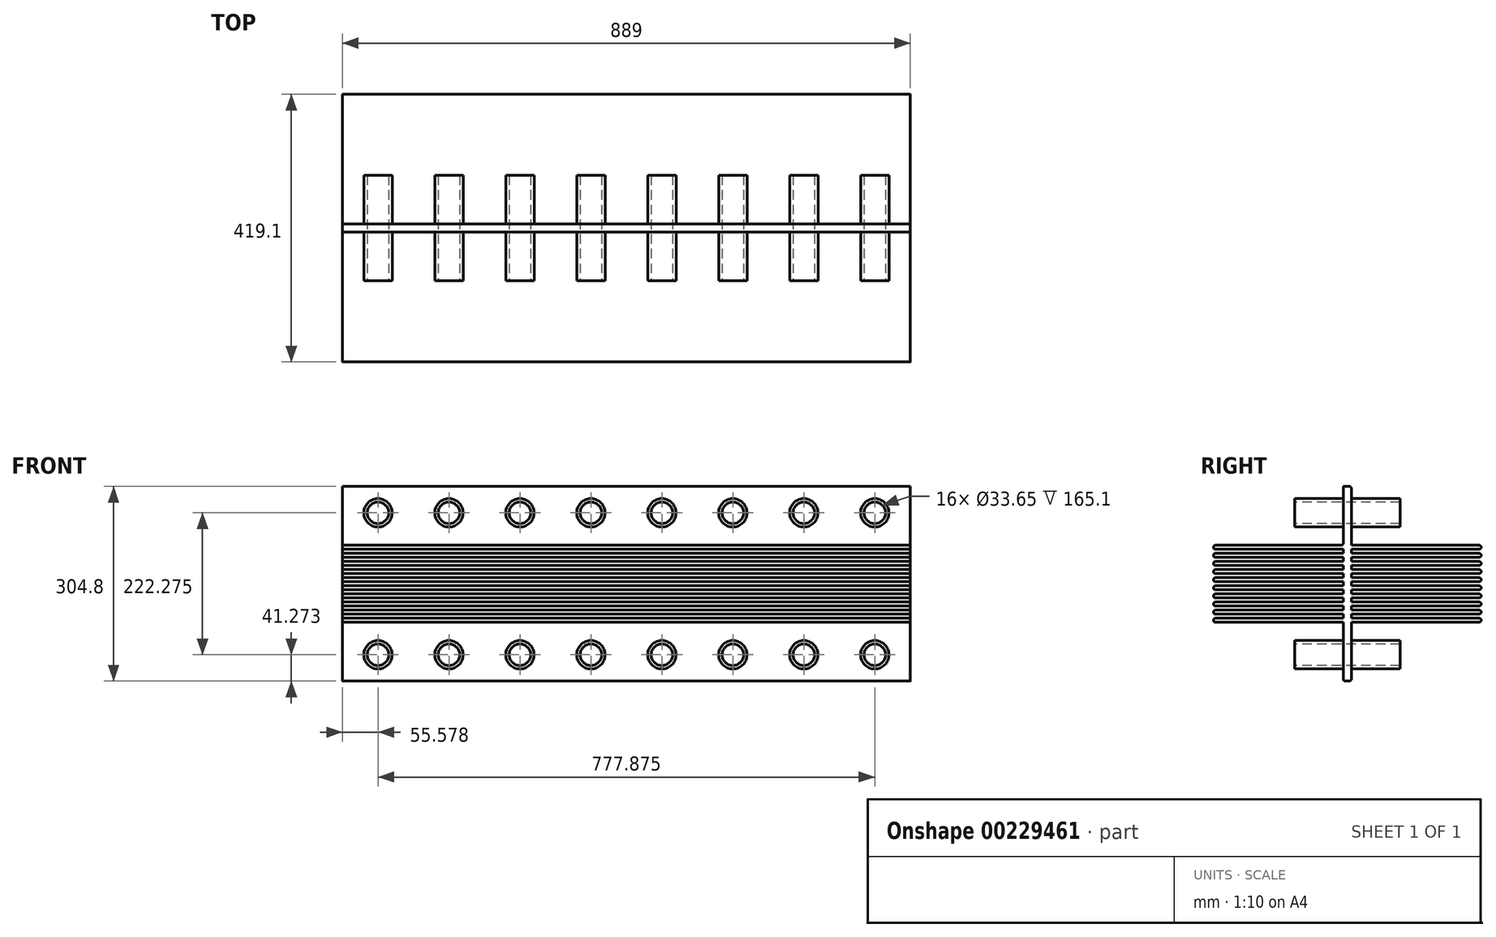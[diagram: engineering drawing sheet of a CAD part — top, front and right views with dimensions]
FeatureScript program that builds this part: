
annotation { "Feature Type Name" : "Feature", "Feature Type Description" : "" }
export const myFeature = defineFeature(function(context is Context, id is Id, definition is map)
    precondition{}
    {
        {
            var Q0;
            Q0=qCreatedBy(makeId("Front.planeOp"),FACE);
            var sketch = newSketch(context, id + "F0", { "sketchPlane" : qUnion([Q0])});
            skLineSegment(sketch, "E0.bottom", {"start": v(-681.77, 148.66) * mm, "end": v(207.23, 148.66) * mm});
            skLineSegment(sketch, "E0.top", {"start": v(-681.77, -156.14) * mm, "end": v(207.23, -156.14) * mm});
            skLineSegment(sketch, "E0.left", {"start": v(-681.77, 148.66) * mm, "end": v(-681.77, -156.14) * mm});
            skLineSegment(sketch, "E0.right", {"start": v(207.23, 148.66) * mm, "end": v(207.23, -156.14) * mm});
            skSolve(sketch);
        }
        {
            var Q0;
            Q0=makeQuery(id+"F0.imprint","IMPRINT",FACE,{"disambiguationData":[TD([[makeQuery(id+"F0.imprint","IMPRINT",EDGE,{"derivedFrom":sQuery(id+"F0.wireOp",EDGE,"E0.bottom")}),-1.0]])]});
            extrude(context, id + "F1", {"entities" : qUnion([Q0]), "depth" : 12.7 * mm});
        }
        {
            var Q0;
            Q0=makeQuery(id+"F1.opExtrude","CAP_FACE",FACE,{"disambiguationData":[OSD([sQuery(id+"F0.wireOp",EDGE,"E0.bottom"),sQuery(id+"F0.wireOp",EDGE,"E0.top"),sQuery(id+"F0.wireOp",EDGE,"E0.left"),sQuery(id+"F0.wireOp",EDGE,"E0.right")])],"isStart":false});
            var sketch = newSketch(context, id + "F2", { "sketchPlane" : qUnion([Q0])});
            skPoint(sketch, "E1", {"position": v(-626.2, -114.87) * mm});
            skPoint(sketch, "E2.0.1.0", {"position": v(-626.2, 107.4) * mm});
            skPoint(sketch, "E2.1.0.0", {"position": v(-515.07, -114.87) * mm});
            skPoint(sketch, "E2.1.1.0", {"position": v(-515.07, 107.4) * mm});
            skPoint(sketch, "E2.2.0.0", {"position": v(-403.94, -114.87) * mm});
            skPoint(sketch, "E2.2.1.0", {"position": v(-403.94, 107.4) * mm});
            skPoint(sketch, "E2.3.0.0", {"position": v(-292.82, -114.87) * mm});
            skPoint(sketch, "E2.3.1.0", {"position": v(-292.82, 107.4) * mm});
            skPoint(sketch, "E2.4.0.0", {"position": v(-181.7, -114.87) * mm});
            skPoint(sketch, "E2.4.1.0", {"position": v(-181.7, 107.4) * mm});
            skPoint(sketch, "E2.5.0.0", {"position": v(-70.57, -114.87) * mm});
            skPoint(sketch, "E2.5.1.0", {"position": v(-70.57, 107.4) * mm});
            skPoint(sketch, "E2.6.0.0", {"position": v(40.56, -114.87) * mm});
            skPoint(sketch, "E2.6.1.0", {"position": v(40.56, 107.4) * mm});
            skPoint(sketch, "E2.7.0.0", {"position": v(151.68, -114.87) * mm});
            skPoint(sketch, "E2.7.1.0", {"position": v(151.68, 107.4) * mm});
            skLineSegment(sketch, "E2.direction1", {"start": v(-626.2, -114.87) * mm, "end": v(-515.07, -114.87) * mm, "construction": true});
            skLineSegment(sketch, "E2.direction2", {"start": v(-626.2, -114.87) * mm, "end": v(-626.2, 107.4) * mm, "construction": true});
            skSolve(sketch);
        }
        {
            var Q0;
            Q0=sQuery(id+"F2.wireOp",VERTEX,"E2.0.1.0");
            var Q1;
            Q1=sQuery(id+"F2.wireOp",VERTEX,"E2.1.1.0");
            var Q2;
            Q2=sQuery(id+"F2.wireOp",VERTEX,"E2.2.1.0");
            var Q3;
            Q3=sQuery(id+"F2.wireOp",VERTEX,"E2.3.1.0");
            var Q4;
            Q4=sQuery(id+"F2.wireOp",VERTEX,"E2.4.1.0");
            var Q5;
            Q5=sQuery(id+"F2.wireOp",VERTEX,"E2.5.1.0");
            var Q6;
            Q6=sQuery(id+"F2.wireOp",VERTEX,"E2.6.1.0");
            var Q7;
            Q7=sQuery(id+"F2.wireOp",VERTEX,"E2.7.1.0");
            var Q8;
            Q8=sQuery(id+"F2.wireOp",VERTEX,"E2.7.0.0");
            var Q9;
            Q9=sQuery(id+"F2.wireOp",VERTEX,"E2.6.0.0");
            var Q10;
            Q10=sQuery(id+"F2.wireOp",VERTEX,"E2.5.0.0");
            var Q11;
            Q11=sQuery(id+"F2.wireOp",VERTEX,"E2.4.0.0");
            var Q12;
            Q12=sQuery(id+"F2.wireOp",VERTEX,"E2.3.0.0");
            var Q13;
            Q13=sQuery(id+"F2.wireOp",VERTEX,"E2.2.0.0");
            var Q14;
            Q14=sQuery(id+"F2.wireOp",VERTEX,"E1");
            var Q15;
            Q15=sQuery(id+"F2.wireOp",VERTEX,"E2.1.0.0");
            var Q16;
            Q16=makeQuery(id+"F1.opExtrude","SWEPT_BODY",BODY,{"disambiguationData":[OSD([sQuery(id+"F0.wireOp",EDGE,"E0.bottom"),sQuery(id+"F0.wireOp",EDGE,"E0.top"),sQuery(id+"F0.wireOp",EDGE,"E0.left"),sQuery(id+"F0.wireOp",EDGE,"E0.right")])]});
            hole(context, id + "F3", {"style" : HoleStyle.SIMPLE, "endStyle" : HoleEndStyle.THROUGH, "holeDiameter" : 33.65 * mm, "locations" : qUnion([Q0, Q1, Q2, Q3, Q4, Q5, Q6, Q7, Q8, Q9, Q10, Q11, Q12, Q13, Q14, Q15]), "scope" : qUnion([Q16]), "isTappedThrough" : true});
        }
        {
            var Q0;
            Q0=makeQuery(id+"F1.opExtrude","SWEPT_FACE",FACE,{"disambiguationData":[OSD([sQuery(id+"F0.wireOp",EDGE,"E0.right")])]});
            var sketch = newSketch(context, id + "F4", { "sketchPlane" : qUnion([Q0])});
            skLineSegment(sketch, "E3", {"start": v(-6.35, -156.14) * mm, "end": v(-6.35, 148.66) * mm, "construction": true});
            skLineSegment(sketch, "E4", {"start": v(-12.7, -3.74) * mm, "end": v(-116.38, -3.74) * mm, "construction": true});
            skLineSegment(sketch, "E5.bottom", {"start": v(-12.7, -6.92) * mm, "end": v(-212.72, -6.92) * mm});
            skLineSegment(sketch, "E5.top", {"start": v(-12.7, -13.27) * mm, "end": v(-212.72, -13.27) * mm});
            skLineSegment(sketch, "E5.left", {"start": v(-12.7, -6.92) * mm, "end": v(-12.7, -13.27) * mm});
            skLineSegment(sketch, "E5.right", {"start": v(-215.9, -10.1) * mm, "end": v(-215.9, -10.1) * mm});
            skLineSegment(sketch, "E6.bottom", {"start": v(-12.7, -19.62) * mm, "end": v(-212.72, -19.62) * mm});
            skLineSegment(sketch, "E6.top", {"start": v(-12.7, -25.97) * mm, "end": v(-212.72, -25.97) * mm});
            skLineSegment(sketch, "E6.left", {"start": v(-12.7, -19.62) * mm, "end": v(-12.7, -25.97) * mm});
            skLineSegment(sketch, "E6.right", {"start": v(-215.9, -22.8) * mm, "end": v(-215.9, -22.8) * mm});
            skLineSegment(sketch, "E7.bottom", {"start": v(-12.7, -32.32) * mm, "end": v(-212.72, -32.32) * mm});
            skLineSegment(sketch, "E7.top", {"start": v(-12.7, -38.67) * mm, "end": v(-212.72, -38.67) * mm});
            skLineSegment(sketch, "E7.left", {"start": v(-12.7, -32.32) * mm, "end": v(-12.7, -38.67) * mm});
            skLineSegment(sketch, "E7.right", {"start": v(-215.9, -35.5) * mm, "end": v(-215.9, -35.5) * mm});
            skLineSegment(sketch, "E8.bottom", {"start": v(-12.7, -45.02) * mm, "end": v(-212.72, -45.02) * mm});
            skLineSegment(sketch, "E8.top", {"start": v(-12.7, -51.37) * mm, "end": v(-212.72, -51.37) * mm});
            skLineSegment(sketch, "E8.left", {"start": v(-12.7, -45.02) * mm, "end": v(-12.7, -51.37) * mm});
            skLineSegment(sketch, "E8.right", {"start": v(-215.9, -48.2) * mm, "end": v(-215.9, -48.2) * mm});
            skLineSegment(sketch, "E9.bottom", {"start": v(-12.7, -57.72) * mm, "end": v(-212.72, -57.72) * mm});
            skLineSegment(sketch, "E9.top", {"start": v(-12.7, -64.07) * mm, "end": v(-212.72, -64.07) * mm});
            skLineSegment(sketch, "E9.left", {"start": v(-12.7, -57.72) * mm, "end": v(-12.7, -64.07) * mm});
            skLineSegment(sketch, "E9.right", {"start": v(-215.9, -60.9) * mm, "end": v(-215.9, -60.9) * mm});
            skLineSegment(sketch, "E10.MirrorCS", {"start": v(-12.7, -0.57) * mm, "end": v(-212.72, -0.57) * mm});
            skLineSegment(sketch, "E11.MirrorCS", {"start": v(-12.7, 5.78) * mm, "end": v(-212.72, 5.78) * mm});
            skLineSegment(sketch, "E12.MirrorCS", {"start": v(-215.9, 2.6) * mm, "end": v(-215.9, 2.6) * mm});
            skLineSegment(sketch, "E13.MirrorCS", {"start": v(-12.7, -0.57) * mm, "end": v(-12.7, 5.78) * mm});
            skLineSegment(sketch, "E14.MirrorCS", {"start": v(-12.7, 12.13) * mm, "end": v(-12.7, 18.48) * mm});
            skLineSegment(sketch, "E15.MirrorCS", {"start": v(-12.7, 12.13) * mm, "end": v(-212.72, 12.13) * mm});
            skLineSegment(sketch, "E16.MirrorCS", {"start": v(-12.7, 18.48) * mm, "end": v(-212.72, 18.48) * mm});
            skLineSegment(sketch, "E17.MirrorCS", {"start": v(-12.7, 24.83) * mm, "end": v(-212.72, 24.83) * mm});
            skLineSegment(sketch, "E18.MirrorCS", {"start": v(-12.7, 31.18) * mm, "end": v(-212.72, 31.18) * mm});
            skLineSegment(sketch, "E19.MirrorCS", {"start": v(-12.7, 24.83) * mm, "end": v(-12.7, 31.18) * mm});
            skLineSegment(sketch, "E20.MirrorCS", {"start": v(-12.7, 37.53) * mm, "end": v(-212.72, 37.53) * mm});
            skLineSegment(sketch, "E21.MirrorCS", {"start": v(-12.7, 43.88) * mm, "end": v(-212.72, 43.88) * mm});
            skLineSegment(sketch, "E22.MirrorCS", {"start": v(-12.7, 37.53) * mm, "end": v(-12.7, 43.88) * mm});
            skLineSegment(sketch, "E23.MirrorCS", {"start": v(-12.7, 50.23) * mm, "end": v(-12.7, 56.58) * mm});
            skLineSegment(sketch, "E24.MirrorCS", {"start": v(-12.7, 50.23) * mm, "end": v(-212.72, 50.23) * mm});
            skLineSegment(sketch, "E25.MirrorCS", {"start": v(-12.7, 56.58) * mm, "end": v(-212.72, 56.58) * mm});
            skLineSegment(sketch, "E26.MirrorCS", {"start": v(-215.9, 15.3) * mm, "end": v(-215.9, 15.3) * mm});
            skLineSegment(sketch, "E27.MirrorCS", {"start": v(-215.9, 28) * mm, "end": v(-215.9, 28) * mm});
            skLineSegment(sketch, "E28.MirrorCS", {"start": v(-215.9, 40.7) * mm, "end": v(-215.9, 40.7) * mm});
            skLineSegment(sketch, "E29.MirrorCS", {"start": v(-215.9, 53.4) * mm, "end": v(-215.9, 53.4) * mm});
            skLineSegment(sketch, "E30.MirrorCS", {"start": v(0, 56.58) * mm, "end": v(200.02, 56.58) * mm});
            skLineSegment(sketch, "E31.MirrorCS", {"start": v(0, 50.23) * mm, "end": v(200.03, 50.23) * mm});
            skLineSegment(sketch, "E32.MirrorCS", {"start": v(0, 43.88) * mm, "end": v(200.02, 43.88) * mm});
            skLineSegment(sketch, "E33.MirrorCS", {"start": v(0, 37.53) * mm, "end": v(200.02, 37.53) * mm});
            skLineSegment(sketch, "E34.MirrorCS", {"start": v(0, 31.18) * mm, "end": v(200.02, 31.18) * mm});
            skLineSegment(sketch, "E35.MirrorCS", {"start": v(0, 24.83) * mm, "end": v(200.02, 24.83) * mm});
            skLineSegment(sketch, "E36.MirrorCS", {"start": v(0, 18.48) * mm, "end": v(200.02, 18.48) * mm});
            skLineSegment(sketch, "E37.MirrorCS", {"start": v(0, 12.13) * mm, "end": v(200.02, 12.13) * mm});
            skLineSegment(sketch, "E38.MirrorCS", {"start": v(0, 5.78) * mm, "end": v(200.02, 5.78) * mm});
            skLineSegment(sketch, "E39.MirrorCS", {"start": v(0, -0.57) * mm, "end": v(200.03, -0.57) * mm});
            skLineSegment(sketch, "E40.MirrorCS", {"start": v(0, -6.92) * mm, "end": v(200.03, -6.92) * mm});
            skLineSegment(sketch, "E41.MirrorCS", {"start": v(0, -13.27) * mm, "end": v(200.02, -13.27) * mm});
            skLineSegment(sketch, "E42.MirrorCS", {"start": v(0, -25.97) * mm, "end": v(200.02, -25.97) * mm});
            skLineSegment(sketch, "E43.MirrorCS", {"start": v(0, -19.62) * mm, "end": v(200.02, -19.62) * mm});
            skLineSegment(sketch, "E44.MirrorCS", {"start": v(0, -32.32) * mm, "end": v(200.02, -32.32) * mm});
            skLineSegment(sketch, "E45.MirrorCS", {"start": v(0, -38.67) * mm, "end": v(200.02, -38.67) * mm});
            skLineSegment(sketch, "E46.MirrorCS", {"start": v(0, -45.02) * mm, "end": v(200.02, -45.02) * mm});
            skLineSegment(sketch, "E47.MirrorCS", {"start": v(0, -51.37) * mm, "end": v(200.03, -51.37) * mm});
            skLineSegment(sketch, "E48.MirrorCS", {"start": v(0, -57.72) * mm, "end": v(200.03, -57.72) * mm});
            skLineSegment(sketch, "E49.MirrorCS", {"start": v(0, -64.07) * mm, "end": v(200.02, -64.07) * mm});
            skLineSegment(sketch, "E50.MirrorCS", {"start": v(203.2, 53.4) * mm, "end": v(203.2, 53.4) * mm});
            skLineSegment(sketch, "E51.MirrorCS", {"start": v(203.2, 40.7) * mm, "end": v(203.2, 40.7) * mm});
            skLineSegment(sketch, "E52.MirrorCS", {"start": v(203.2, 28) * mm, "end": v(203.2, 28) * mm});
            skLineSegment(sketch, "E53.MirrorCS", {"start": v(203.2, 15.3) * mm, "end": v(203.2, 15.3) * mm});
            skLineSegment(sketch, "E54.MirrorCS", {"start": v(203.2, 2.6) * mm, "end": v(203.2, 2.6) * mm});
            skLineSegment(sketch, "E55.MirrorCS", {"start": v(203.2, -10.1) * mm, "end": v(203.2, -10.1) * mm});
            skLineSegment(sketch, "E56.MirrorCS", {"start": v(203.2, -22.8) * mm, "end": v(203.2, -22.8) * mm});
            skLineSegment(sketch, "E57.MirrorCS", {"start": v(203.2, -35.5) * mm, "end": v(203.2, -35.5) * mm});
            skLineSegment(sketch, "E58.MirrorCS", {"start": v(203.2, -48.2) * mm, "end": v(203.2, -48.2) * mm});
            skLineSegment(sketch, "E59.MirrorCS", {"start": v(203.2, -60.9) * mm, "end": v(203.2, -60.9) * mm});
            skLineSegment(sketch, "E60.MirrorCS", {"start": v(0, 50.23) * mm, "end": v(0, 56.58) * mm});
            skLineSegment(sketch, "E61.MirrorCS", {"start": v(0, 37.53) * mm, "end": v(0, 43.88) * mm});
            skLineSegment(sketch, "E62.MirrorCS", {"start": v(0, 24.83) * mm, "end": v(0, 31.18) * mm});
            skLineSegment(sketch, "E63.MirrorCS", {"start": v(0, 12.13) * mm, "end": v(0, 18.48) * mm});
            skLineSegment(sketch, "E64.MirrorCS", {"start": v(0, -0.57) * mm, "end": v(0, 5.78) * mm});
            skLineSegment(sketch, "E65.MirrorCS", {"start": v(0, -6.92) * mm, "end": v(0, -13.27) * mm});
            skLineSegment(sketch, "E66.MirrorCS", {"start": v(0, -19.62) * mm, "end": v(0, -25.97) * mm});
            skLineSegment(sketch, "E67.MirrorCS", {"start": v(0, -32.32) * mm, "end": v(0, -38.67) * mm});
            skLineSegment(sketch, "E68.MirrorCS", {"start": v(0, -45.02) * mm, "end": v(0, -51.37) * mm});
            skLineSegment(sketch, "E69.MirrorCS", {"start": v(0, -57.72) * mm, "end": v(0, -64.07) * mm});
            skPoint(sketch, "E70.visualSharp", {"position": v(203.2, 56.58) * mm});
            skArc(sketch, "E70.filletArc", {"start": v(203.2, 53.4) * mm, "mid": v(202.27, 55.65) * mm, "end": v(200.02, 56.58) * mm});
            skPoint(sketch, "E71.visualSharp", {"position": v(203.2, 50.23) * mm});
            skArc(sketch, "E71.filletArc", {"start": v(200.03, 50.23) * mm, "mid": v(202.27, 51.16) * mm, "end": v(203.2, 53.4) * mm});
            skPoint(sketch, "E72.visualSharp", {"position": v(203.2, 43.88) * mm});
            skArc(sketch, "E72.filletArc", {"start": v(203.2, 40.7) * mm, "mid": v(202.27, 42.95) * mm, "end": v(200.02, 43.88) * mm});
            skPoint(sketch, "E73.visualSharp", {"position": v(203.2, 37.53) * mm});
            skArc(sketch, "E73.filletArc", {"start": v(200.02, 37.53) * mm, "mid": v(202.27, 38.46) * mm, "end": v(203.2, 40.7) * mm});
            skPoint(sketch, "E74.visualSharp", {"position": v(203.2, 31.18) * mm});
            skArc(sketch, "E74.filletArc", {"start": v(203.2, 28) * mm, "mid": v(202.27, 30.25) * mm, "end": v(200.02, 31.18) * mm});
            skPoint(sketch, "E75.visualSharp", {"position": v(203.2, 24.83) * mm});
            skArc(sketch, "E75.filletArc", {"start": v(200.02, 24.83) * mm, "mid": v(202.27, 25.76) * mm, "end": v(203.2, 28) * mm});
            skPoint(sketch, "E76.visualSharp", {"position": v(203.2, 18.48) * mm});
            skArc(sketch, "E76.filletArc", {"start": v(203.2, 15.3) * mm, "mid": v(202.27, 17.55) * mm, "end": v(200.02, 18.48) * mm});
            skPoint(sketch, "E77.visualSharp", {"position": v(203.2, 12.13) * mm});
            skArc(sketch, "E77.filletArc", {"start": v(200.02, 12.13) * mm, "mid": v(202.27, 13.06) * mm, "end": v(203.2, 15.3) * mm});
            skPoint(sketch, "E78.visualSharp", {"position": v(203.2, 5.78) * mm});
            skArc(sketch, "E78.filletArc", {"start": v(203.2, 2.6) * mm, "mid": v(202.27, 4.85) * mm, "end": v(200.02, 5.78) * mm});
            skPoint(sketch, "E79.visualSharp", {"position": v(203.2, -0.57) * mm});
            skArc(sketch, "E79.filletArc", {"start": v(200.03, -0.57) * mm, "mid": v(202.27, 0.36) * mm, "end": v(203.2, 2.6) * mm});
            skPoint(sketch, "E80.visualSharp", {"position": v(203.2, -6.92) * mm});
            skArc(sketch, "E80.filletArc", {"start": v(203.2, -10.1) * mm, "mid": v(202.27, -7.85) * mm, "end": v(200.03, -6.92) * mm});
            skPoint(sketch, "E81.visualSharp", {"position": v(203.2, -13.27) * mm});
            skArc(sketch, "E81.filletArc", {"start": v(200.02, -13.27) * mm, "mid": v(202.27, -12.34) * mm, "end": v(203.2, -10.1) * mm});
            skPoint(sketch, "E82.visualSharp", {"position": v(203.2, -19.62) * mm});
            skArc(sketch, "E82.filletArc", {"start": v(203.2, -22.8) * mm, "mid": v(202.27, -20.55) * mm, "end": v(200.02, -19.62) * mm});
            skPoint(sketch, "E83.visualSharp", {"position": v(203.2, -25.97) * mm});
            skArc(sketch, "E83.filletArc", {"start": v(200.02, -25.97) * mm, "mid": v(202.27, -25.04) * mm, "end": v(203.2, -22.8) * mm});
            skPoint(sketch, "E84.visualSharp", {"position": v(203.2, -32.32) * mm});
            skArc(sketch, "E84.filletArc", {"start": v(203.2, -35.5) * mm, "mid": v(202.27, -33.25) * mm, "end": v(200.02, -32.32) * mm});
            skPoint(sketch, "E85.visualSharp", {"position": v(203.2, -38.67) * mm});
            skArc(sketch, "E85.filletArc", {"start": v(200.02, -38.67) * mm, "mid": v(202.27, -37.74) * mm, "end": v(203.2, -35.5) * mm});
            skPoint(sketch, "E86.visualSharp", {"position": v(203.2, -45.02) * mm});
            skArc(sketch, "E86.filletArc", {"start": v(203.2, -48.2) * mm, "mid": v(202.27, -45.95) * mm, "end": v(200.02, -45.02) * mm});
            skPoint(sketch, "E87.visualSharp", {"position": v(203.2, -51.37) * mm});
            skArc(sketch, "E87.filletArc", {"start": v(200.03, -51.37) * mm, "mid": v(202.27, -50.44) * mm, "end": v(203.2, -48.2) * mm});
            skPoint(sketch, "E88.visualSharp", {"position": v(203.2, -57.72) * mm});
            skArc(sketch, "E88.filletArc", {"start": v(203.2, -60.9) * mm, "mid": v(202.27, -58.65) * mm, "end": v(200.03, -57.72) * mm});
            skPoint(sketch, "E89.visualSharp", {"position": v(203.2, -64.07) * mm});
            skArc(sketch, "E89.filletArc", {"start": v(200.02, -64.07) * mm, "mid": v(202.27, -63.14) * mm, "end": v(203.2, -60.9) * mm});
            skPoint(sketch, "E90.visualSharp", {"position": v(-215.9, 56.58) * mm});
            skArc(sketch, "E90.filletArc", {"start": v(-212.72, 56.58) * mm, "mid": v(-214.97, 55.65) * mm, "end": v(-215.9, 53.4) * mm});
            skPoint(sketch, "E91.visualSharp", {"position": v(-215.9, 50.23) * mm});
            skArc(sketch, "E91.filletArc", {"start": v(-215.9, 53.4) * mm, "mid": v(-214.97, 51.16) * mm, "end": v(-212.72, 50.23) * mm});
            skPoint(sketch, "E92.visualSharp", {"position": v(-215.9, 43.88) * mm});
            skArc(sketch, "E92.filletArc", {"start": v(-212.72, 43.88) * mm, "mid": v(-214.97, 42.95) * mm, "end": v(-215.9, 40.7) * mm});
            skPoint(sketch, "E93.visualSharp", {"position": v(-215.9, 37.53) * mm});
            skArc(sketch, "E93.filletArc", {"start": v(-215.9, 40.7) * mm, "mid": v(-214.97, 38.46) * mm, "end": v(-212.72, 37.53) * mm});
            skPoint(sketch, "E94.visualSharp", {"position": v(-215.9, 31.18) * mm});
            skArc(sketch, "E94.filletArc", {"start": v(-212.72, 31.18) * mm, "mid": v(-214.97, 30.25) * mm, "end": v(-215.9, 28) * mm});
            skPoint(sketch, "E95.visualSharp", {"position": v(-215.9, 24.83) * mm});
            skArc(sketch, "E95.filletArc", {"start": v(-215.9, 28) * mm, "mid": v(-214.97, 25.76) * mm, "end": v(-212.72, 24.83) * mm});
            skPoint(sketch, "E96.visualSharp", {"position": v(-215.9, 18.48) * mm});
            skArc(sketch, "E96.filletArc", {"start": v(-212.72, 18.48) * mm, "mid": v(-214.97, 17.55) * mm, "end": v(-215.9, 15.3) * mm});
            skPoint(sketch, "E97.visualSharp", {"position": v(-215.9, 12.13) * mm});
            skArc(sketch, "E97.filletArc", {"start": v(-215.9, 15.3) * mm, "mid": v(-214.97, 13.06) * mm, "end": v(-212.72, 12.13) * mm});
            skPoint(sketch, "E98.visualSharp", {"position": v(-215.9, 5.78) * mm});
            skArc(sketch, "E98.filletArc", {"start": v(-212.72, 5.78) * mm, "mid": v(-214.97, 4.85) * mm, "end": v(-215.9, 2.6) * mm});
            skPoint(sketch, "E99.visualSharp", {"position": v(-215.9, -0.57) * mm});
            skArc(sketch, "E99.filletArc", {"start": v(-215.9, 2.6) * mm, "mid": v(-214.97, 0.36) * mm, "end": v(-212.72, -0.57) * mm});
            skPoint(sketch, "E100.visualSharp", {"position": v(-215.9, -6.92) * mm});
            skArc(sketch, "E100.filletArc", {"start": v(-212.72, -6.92) * mm, "mid": v(-214.97, -7.85) * mm, "end": v(-215.9, -10.1) * mm});
            skPoint(sketch, "E101.visualSharp", {"position": v(-215.9, -13.27) * mm});
            skArc(sketch, "E101.filletArc", {"start": v(-215.9, -10.1) * mm, "mid": v(-214.97, -12.34) * mm, "end": v(-212.72, -13.27) * mm});
            skPoint(sketch, "E102.visualSharp", {"position": v(-215.9, -19.62) * mm});
            skArc(sketch, "E102.filletArc", {"start": v(-212.72, -19.62) * mm, "mid": v(-214.97, -20.55) * mm, "end": v(-215.9, -22.8) * mm});
            skPoint(sketch, "E103.visualSharp", {"position": v(-215.9, -25.97) * mm});
            skArc(sketch, "E103.filletArc", {"start": v(-215.9, -22.8) * mm, "mid": v(-214.97, -25.04) * mm, "end": v(-212.72, -25.97) * mm});
            skPoint(sketch, "E104.visualSharp", {"position": v(-215.9, -38.67) * mm});
            skArc(sketch, "E104.filletArc", {"start": v(-215.9, -35.5) * mm, "mid": v(-214.97, -37.74) * mm, "end": v(-212.72, -38.67) * mm});
            skPoint(sketch, "E105.visualSharp", {"position": v(-215.9, -32.32) * mm});
            skArc(sketch, "E105.filletArc", {"start": v(-212.72, -32.32) * mm, "mid": v(-214.97, -33.25) * mm, "end": v(-215.9, -35.5) * mm});
            skPoint(sketch, "E106.visualSharp", {"position": v(-215.9, -45.02) * mm});
            skArc(sketch, "E106.filletArc", {"start": v(-212.72, -45.02) * mm, "mid": v(-214.97, -45.95) * mm, "end": v(-215.9, -48.2) * mm});
            skPoint(sketch, "E107.visualSharp", {"position": v(-215.9, -51.37) * mm});
            skArc(sketch, "E107.filletArc", {"start": v(-215.9, -48.2) * mm, "mid": v(-214.97, -50.44) * mm, "end": v(-212.72, -51.37) * mm});
            skPoint(sketch, "E108.visualSharp", {"position": v(-215.9, -57.72) * mm});
            skArc(sketch, "E108.filletArc", {"start": v(-212.72, -57.72) * mm, "mid": v(-214.97, -58.65) * mm, "end": v(-215.9, -60.9) * mm});
            skPoint(sketch, "E109.visualSharp", {"position": v(-215.9, -64.07) * mm});
            skArc(sketch, "E109.filletArc", {"start": v(-215.9, -60.9) * mm, "mid": v(-214.97, -63.14) * mm, "end": v(-212.72, -64.07) * mm});
            skSolve(sketch);
        }
        {
            var Q0;
            Q0 = qSketchRegion(id + "F4", true);
            extrude(context, id + "F5", {"entities" : qUnion([Q0]), "operationType" : NewBodyOperationType.ADD, "oppositeDirection" : true, "depth" : 889 * mm});
        }
        {
            var Q0;
            Q0=makeQuery(id+"F1.opExtrude","CAP_EDGE",EDGE,{"disambiguationData":[OSD([sQuery(id+"F0.wireOp",EDGE,"E0.bottom")])],"isStart":true});
            var Q1;
            Q1=makeQuery(id+"F5.opExtrude","SWEPT_EDGE",EDGE,{"disambiguationData":[OSD([sQuery(id+"F0.wireOp",EDGE,"E0.right"),sQuery(id+"F4.wireOp",EDGE,"E23.MirrorCS"),sQuery(id+"F4.wireOp",EDGE,"E25.MirrorCS")])]});
            var Q2;
            Q2=makeQuery(id+"F1.opExtrude","CAP_EDGE",EDGE,{"disambiguationData":[OSD([sQuery(id+"F0.wireOp",EDGE,"E0.top")])],"isStart":true});
            var Q3;
            Q3=makeQuery(id+"F1.opExtrude","CAP_EDGE",EDGE,{"disambiguationData":[OSD([sQuery(id+"F0.wireOp",EDGE,"E0.top")])],"isStart":false});
            fillet(context, id + "F6", {"entities" : qUnion([Q0, Q1, Q2, Q3]), "radius" : 3.17 * mm, "tangentPropagation" : true, "allowEdgeOverflow" : false});
        }
        {
            var Q0;
            {var subQ85=sQuery(id+"F0.wireOp",EDGE,"E0.right");var subQ86=sQuery(id+"F0.wireOp",EDGE,"E0.top");var subQ87=sQuery(id+"F0.wireOp",EDGE,"E0.left");Q0=makeQuery(id+"F5.boolean.opBoolean","SPLIT",FACE,{"disambiguationData":[TD([makeQuery(id+"F1.opExtrude","SWEPT_FACE",FACE,{"disambiguationData":[OSD([subQ86])]})])],"derivedFrom":makeQuery(id+"F1.opExtrude","CAP_FACE",FACE,{"disambiguationData":[OSD([sQuery(id+"F0.wireOp",EDGE,"E0.bottom"),subQ86,subQ87,subQ85])],"isStart":true})});}
            var sketch = newSketch(context, id + "F7", { "sketchPlane" : qUnion([Q0])});
            skCircle(sketch, "E110.0", {"center": v(-151.68, -114.87) * mm, "radius": 16.83 * mm});
            skCircle(sketch, "E111", {"center": v(-151.68, -114.87) * mm, "radius": 22.24 * mm});
            skCircle(sketch, "E112.0.1.0", {"center": v(-151.68, 107.4) * mm, "radius": 22.24 * mm});
            skCircle(sketch, "E112.0.1.1", {"center": v(-151.68, 107.4) * mm, "radius": 16.83 * mm});
            skCircle(sketch, "E112.1.0.0", {"center": v(-40.56, -114.87) * mm, "radius": 22.24 * mm});
            skCircle(sketch, "E112.1.0.1", {"center": v(-40.56, -114.87) * mm, "radius": 16.83 * mm});
            skCircle(sketch, "E112.1.1.0", {"center": v(-40.56, 107.4) * mm, "radius": 22.24 * mm});
            skCircle(sketch, "E112.1.1.1", {"center": v(-40.56, 107.4) * mm, "radius": 16.83 * mm});
            skCircle(sketch, "E112.2.0.0", {"center": v(70.57, -114.87) * mm, "radius": 22.24 * mm});
            skCircle(sketch, "E112.2.0.1", {"center": v(70.57, -114.87) * mm, "radius": 16.83 * mm});
            skCircle(sketch, "E112.2.1.0", {"center": v(70.57, 107.4) * mm, "radius": 22.24 * mm});
            skCircle(sketch, "E112.2.1.1", {"center": v(70.57, 107.4) * mm, "radius": 16.83 * mm});
            skCircle(sketch, "E112.3.0.0", {"center": v(181.7, -114.87) * mm, "radius": 22.24 * mm});
            skCircle(sketch, "E112.3.0.1", {"center": v(181.7, -114.87) * mm, "radius": 16.83 * mm});
            skCircle(sketch, "E112.3.1.0", {"center": v(181.7, 107.4) * mm, "radius": 22.24 * mm});
            skCircle(sketch, "E112.3.1.1", {"center": v(181.7, 107.4) * mm, "radius": 16.83 * mm});
            skCircle(sketch, "E112.4.0.0", {"center": v(292.82, -114.87) * mm, "radius": 22.24 * mm});
            skCircle(sketch, "E112.4.0.1", {"center": v(292.82, -114.87) * mm, "radius": 16.83 * mm});
            skCircle(sketch, "E112.4.1.0", {"center": v(292.82, 107.4) * mm, "radius": 22.24 * mm});
            skCircle(sketch, "E112.4.1.1", {"center": v(292.82, 107.4) * mm, "radius": 16.83 * mm});
            skCircle(sketch, "E112.5.0.0", {"center": v(403.94, -114.87) * mm, "radius": 22.24 * mm});
            skCircle(sketch, "E112.5.0.1", {"center": v(403.94, -114.87) * mm, "radius": 16.83 * mm});
            skCircle(sketch, "E112.5.1.0", {"center": v(403.94, 107.4) * mm, "radius": 22.24 * mm});
            skCircle(sketch, "E112.5.1.1", {"center": v(403.94, 107.4) * mm, "radius": 16.83 * mm});
            skCircle(sketch, "E112.6.0.0", {"center": v(515.07, -114.87) * mm, "radius": 22.24 * mm});
            skCircle(sketch, "E112.6.0.1", {"center": v(515.07, -114.87) * mm, "radius": 16.83 * mm});
            skCircle(sketch, "E112.6.1.0", {"center": v(515.07, 107.4) * mm, "radius": 22.24 * mm});
            skCircle(sketch, "E112.6.1.1", {"center": v(515.07, 107.4) * mm, "radius": 16.83 * mm});
            skCircle(sketch, "E112.7.0.0", {"center": v(626.2, -114.87) * mm, "radius": 22.24 * mm});
            skCircle(sketch, "E112.7.0.1", {"center": v(626.2, -114.87) * mm, "radius": 16.83 * mm});
            skCircle(sketch, "E112.7.1.0", {"center": v(626.2, 107.4) * mm, "radius": 22.24 * mm});
            skCircle(sketch, "E112.7.1.1", {"center": v(626.2, 107.4) * mm, "radius": 16.83 * mm});
            skLineSegment(sketch, "E112.direction1", {"start": v(-151.68, -114.87) * mm, "end": v(-40.56, -114.87) * mm, "construction": true});
            skLineSegment(sketch, "E112.direction2", {"start": v(-151.68, -114.87) * mm, "end": v(-151.68, 107.4) * mm, "construction": true});
            skSolve(sketch);
        }
        {
            var Q0;
            Q0 = qSketchRegion(id + "F7", true);
            extrude(context, id + "F8", {"entities" : qUnion([Q0]), "operationType" : NewBodyOperationType.ADD, "depth" : 76.2 * mm});
        }
        {
            var Q0;
            {var subQ90=sQuery(id+"F0.wireOp",EDGE,"E0.left");var subQ91=sQuery(id+"F0.wireOp",EDGE,"E0.right");var subQ92=sQuery(id+"F0.wireOp",EDGE,"E0.bottom");Q0=makeQuery(id+"F5.boolean.opBoolean","SPLIT",FACE,{"disambiguationData":[TD([makeQuery(id+"F1.opExtrude","SWEPT_FACE",FACE,{"disambiguationData":[OSD([subQ92])]})])],"derivedFrom":makeQuery(id+"F1.opExtrude","CAP_FACE",FACE,{"disambiguationData":[OSD([subQ92,sQuery(id+"F0.wireOp",EDGE,"E0.top"),subQ90,subQ91])],"isStart":false})});}
            var sketch = newSketch(context, id + "F9", { "sketchPlane" : qUnion([Q0])});
            skCircle(sketch, "E113.0", {"center": v(-626.2, 107.4) * mm, "radius": 16.83 * mm});
            skCircle(sketch, "E114", {"center": v(-626.2, 107.4) * mm, "radius": 22.24 * mm});
            skCircle(sketch, "E115.0.1.0", {"center": v(-626.2, -114.87) * mm, "radius": 22.24 * mm});
            skCircle(sketch, "E115.0.1.1", {"center": v(-626.2, -114.87) * mm, "radius": 16.83 * mm});
            skCircle(sketch, "E115.1.0.0", {"center": v(-515.07, 107.4) * mm, "radius": 22.24 * mm});
            skCircle(sketch, "E115.1.0.1", {"center": v(-515.07, 107.4) * mm, "radius": 16.83 * mm});
            skCircle(sketch, "E115.1.1.0", {"center": v(-515.07, -114.87) * mm, "radius": 22.24 * mm});
            skCircle(sketch, "E115.1.1.1", {"center": v(-515.07, -114.87) * mm, "radius": 16.83 * mm});
            skCircle(sketch, "E115.2.0.0", {"center": v(-403.94, 107.4) * mm, "radius": 22.24 * mm});
            skCircle(sketch, "E115.2.0.1", {"center": v(-403.94, 107.4) * mm, "radius": 16.83 * mm});
            skCircle(sketch, "E115.2.1.0", {"center": v(-403.94, -114.87) * mm, "radius": 22.24 * mm});
            skCircle(sketch, "E115.2.1.1", {"center": v(-403.94, -114.87) * mm, "radius": 16.83 * mm});
            skCircle(sketch, "E115.3.0.0", {"center": v(-292.82, 107.4) * mm, "radius": 22.24 * mm});
            skCircle(sketch, "E115.3.0.1", {"center": v(-292.82, 107.4) * mm, "radius": 16.83 * mm});
            skCircle(sketch, "E115.3.1.0", {"center": v(-292.82, -114.87) * mm, "radius": 22.24 * mm});
            skCircle(sketch, "E115.3.1.1", {"center": v(-292.82, -114.87) * mm, "radius": 16.83 * mm});
            skCircle(sketch, "E115.4.0.0", {"center": v(-181.7, 107.4) * mm, "radius": 22.24 * mm});
            skCircle(sketch, "E115.4.0.1", {"center": v(-181.7, 107.4) * mm, "radius": 16.83 * mm});
            skCircle(sketch, "E115.4.1.0", {"center": v(-181.7, -114.87) * mm, "radius": 22.24 * mm});
            skCircle(sketch, "E115.4.1.1", {"center": v(-181.7, -114.87) * mm, "radius": 16.83 * mm});
            skCircle(sketch, "E115.5.0.0", {"center": v(-70.57, 107.4) * mm, "radius": 22.24 * mm});
            skCircle(sketch, "E115.5.0.1", {"center": v(-70.57, 107.4) * mm, "radius": 16.83 * mm});
            skCircle(sketch, "E115.5.1.0", {"center": v(-70.57, -114.87) * mm, "radius": 22.24 * mm});
            skCircle(sketch, "E115.5.1.1", {"center": v(-70.57, -114.87) * mm, "radius": 16.83 * mm});
            skCircle(sketch, "E115.6.0.0", {"center": v(40.56, 107.4) * mm, "radius": 22.24 * mm});
            skCircle(sketch, "E115.6.0.1", {"center": v(40.56, 107.4) * mm, "radius": 16.83 * mm});
            skCircle(sketch, "E115.6.1.0", {"center": v(40.56, -114.87) * mm, "radius": 22.24 * mm});
            skCircle(sketch, "E115.6.1.1", {"center": v(40.56, -114.87) * mm, "radius": 16.83 * mm});
            skCircle(sketch, "E115.7.0.0", {"center": v(151.68, 107.4) * mm, "radius": 22.24 * mm});
            skCircle(sketch, "E115.7.0.1", {"center": v(151.68, 107.4) * mm, "radius": 16.83 * mm});
            skCircle(sketch, "E115.7.1.0", {"center": v(151.68, -114.87) * mm, "radius": 22.24 * mm});
            skCircle(sketch, "E115.7.1.1", {"center": v(151.68, -114.87) * mm, "radius": 16.83 * mm});
            skLineSegment(sketch, "E115.direction1", {"start": v(-626.2, 107.4) * mm, "end": v(-515.07, 107.4) * mm, "construction": true});
            skLineSegment(sketch, "E115.direction2", {"start": v(-626.2, 107.4) * mm, "end": v(-626.2, -114.87) * mm, "construction": true});
            skSolve(sketch);
        }
        {
            var Q0;
            Q0 = qSketchRegion(id + "F9", true);
            extrude(context, id + "F10", {"entities" : qUnion([Q0]), "operationType" : NewBodyOperationType.ADD, "depth" : 76.2 * mm});
        }
    });
